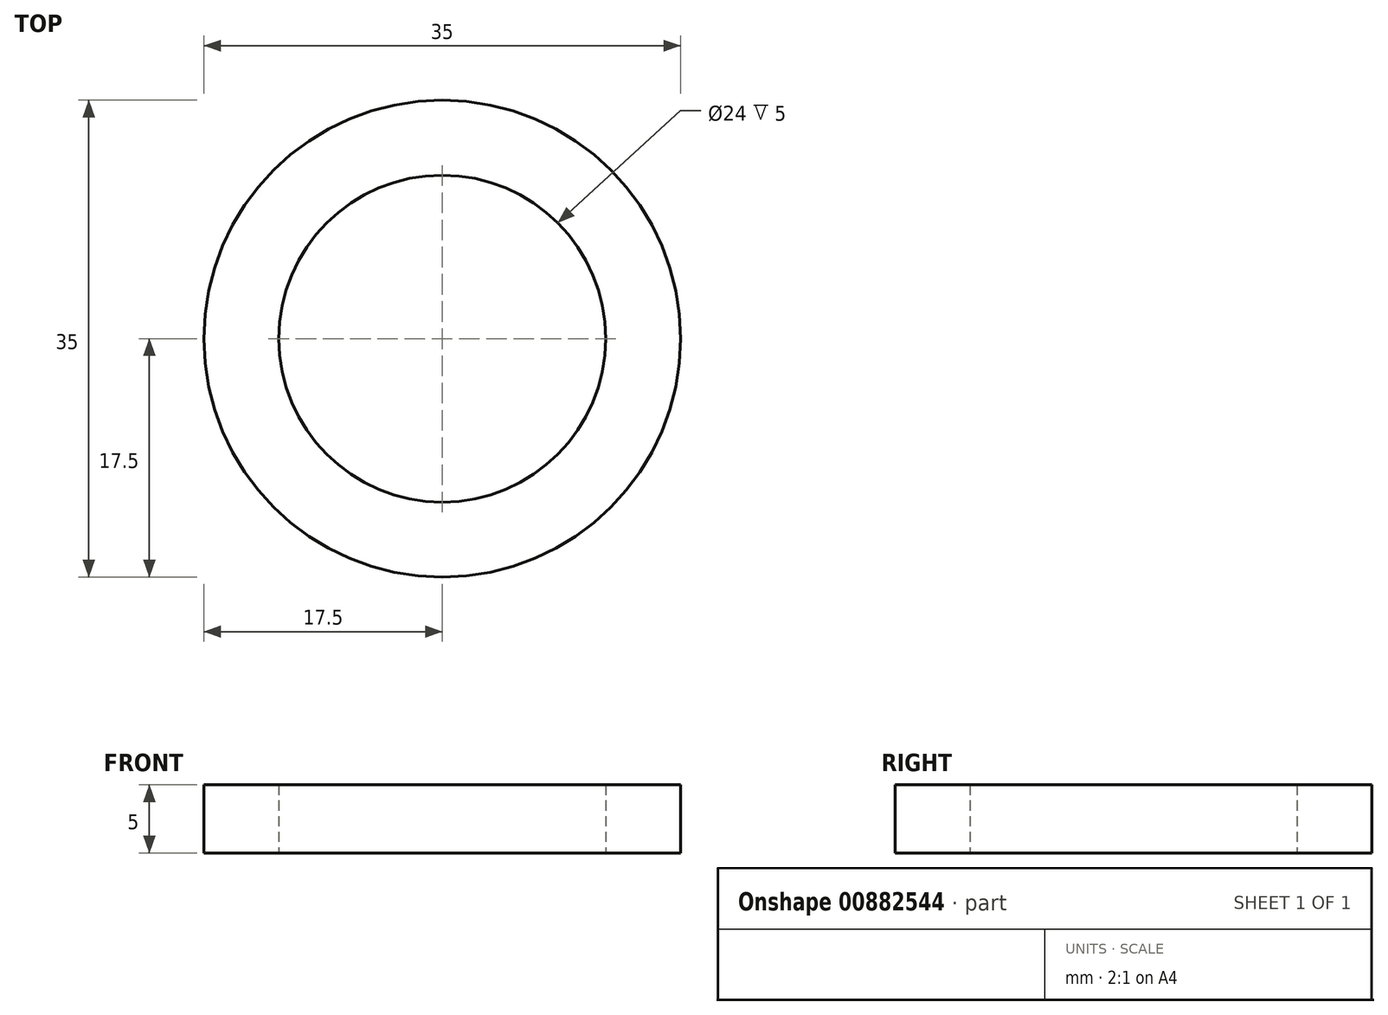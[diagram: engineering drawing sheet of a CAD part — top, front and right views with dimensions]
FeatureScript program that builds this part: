
annotation { "Feature Type Name" : "Feature", "Feature Type Description" : "" }
export const myFeature = defineFeature(function(context is Context, id is Id, definition is map)
    precondition{}
    {
        {
            var Q0;
            Q0=qCreatedBy(makeId("Top.planeOp"),FACE);
            var sketch = newSketch(context, id + "F0", { "sketchPlane" : qUnion([Q0])});
            skCircle(sketch, "E0", {"center": v(0, 0) * mm, "radius": 12 * mm});
            skCircle(sketch, "E1", {"center": v(0, 0) * mm, "radius": 17.5 * mm});
            skSolve(sketch);
        }
        {
            var Q0;
            Q0=qSketchRegion(id+"F0",true);
            extrude(context, id + "F1", {"entities" : qUnion([Q0]), "depth" : 5 * mm, "offsetDistance" : 25 * mm});
        }
    });
